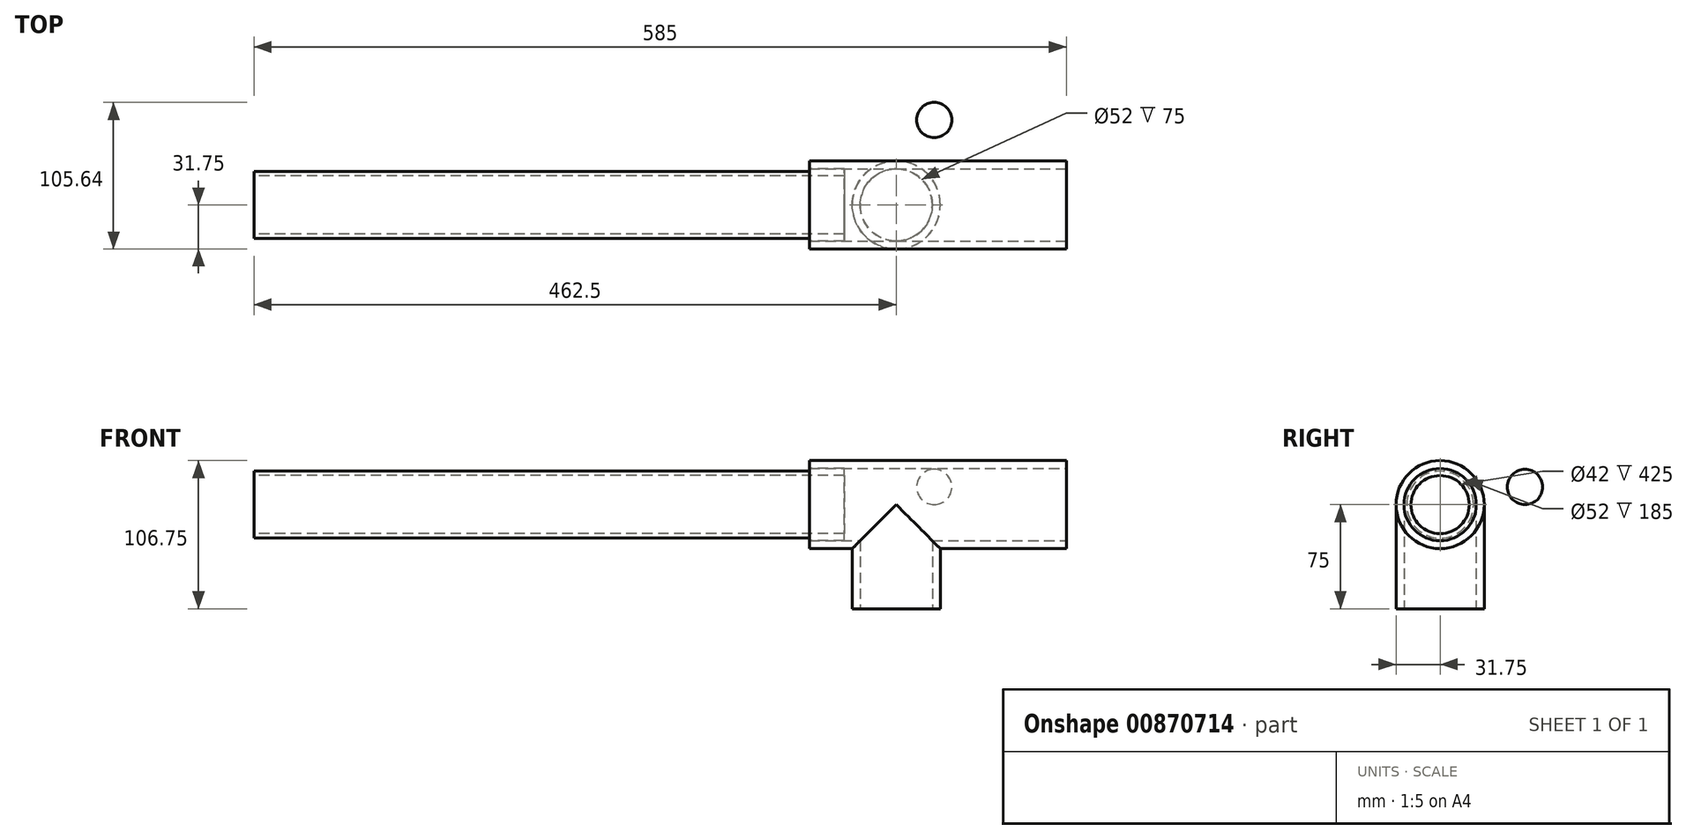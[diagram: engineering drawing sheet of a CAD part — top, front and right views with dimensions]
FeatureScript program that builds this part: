
annotation { "Feature Type Name" : "Feature", "Feature Type Description" : "" }
export const myFeature = defineFeature(function(context is Context, id is Id, definition is map)
    precondition{}
    {
        {
            var Q0;
            Q0=qCreatedBy(makeId("Right.planeOp"),FACE);
            var sketch = newSketch(context, id + "F0", { "sketchPlane" : qUnion([Q0])});
            skCircle(sketch, "E0", {"center": v(0, 0) * mm, "radius": 26 * mm});
            skCircle(sketch, "E1", {"center": v(0, 0) * mm, "radius": 31.75 * mm});
            skSolve(sketch);
        }
        {
            var Q0;
            Q0=makeQuery(id+"F0.imprint","IMPRINT",FACE,{"disambiguationData":[TD([[makeQuery(id+"F0.imprint","IMPRINT",EDGE,{"derivedFrom":sQuery(id+"F0.wireOp",EDGE,"E0")}),-1.0]])]});
            extrude(context, id + "F1", {"entities" : qUnion([Q0]), "oppositeDirection" : true, "depth" : 25 * mm, "offsetDistance" : 25 * mm});
        }
        {
            var Q0;
            Q0=makeQuery(id+"F1.opExtrude","CAP_FACE",FACE,{"disambiguationData":[OSD([sQuery(id+"F0.wireOp",EDGE,"E0"),sQuery(id+"F0.wireOp",EDGE,"E1")])],"isStart":false});
            extrude(context, id + "F2", {"entities" : qUnion([Q0]), "operationType" : NewBodyOperationType.ADD, "depth" : 75 * mm, "offsetDistance" : 25 * mm});
        }
        {
            var Q0;
            Q0=makeQuery(id+"F2.opExtrude","CAP_FACE",FACE,{"disambiguationData":[OSD([sQuery(id+"F0.wireOp",EDGE,"E0"),sQuery(id+"F0.wireOp",EDGE,"E1")])],"isStart":false});
            extrude(context, id + "F3", {"entities" : qUnion([Q0]), "operationType" : NewBodyOperationType.ADD, "depth" : 25 * mm, "offsetDistance" : 25 * mm});
        }
        {
            var Q0;
            Q0=qCreatedBy(makeId("Top.planeOp"),FACE);
            var sketch = newSketch(context, id + "F4", { "sketchPlane" : qUnion([Q0])});
            skCircle(sketch, "E2", {"center": v(-62.5, 0) * mm, "radius": 31.75 * mm});
            skSolve(sketch);
        }
        {
            var Q0;
            Q0=qCreatedBy(makeId("Top.planeOp"),FACE);
            var sketch = newSketch(context, id + "F5", { "sketchPlane" : qUnion([Q0])});
            skCircle(sketch, "E3", {"center": v(-62.5, 0) * mm, "radius": 26 * mm});
            skSolve(sketch);
        }
        {
            var Q0;
            Q0=makeQuery(id+"F3.opExtrude","CAP_FACE",FACE,{"disambiguationData":[OSD([sQuery(id+"F0.wireOp",EDGE,"E0"),sQuery(id+"F0.wireOp",EDGE,"E1")])],"isStart":false});
            var sketch = newSketch(context, id + "F6", { "sketchPlane" : qUnion([Q0])});
            skCircle(sketch, "E4", {"center": v(0, 0) * mm, "radius": 26 * mm});
            skSolve(sketch);
        }
        {
            var Q0;
            Q0=makeQuery(id+"F6.imprint","IMPRINT",FACE,{"disambiguationData":[TD([[makeQuery(id+"F6.imprint","IMPRINT",EDGE,{"derivedFrom":sQuery(id+"F6.wireOp",EDGE,"E4")}),-1.0]])]});
            extrude(context, id + "F7", {"entities" : qUnion([Q0]), "operationType" : NewBodyOperationType.REMOVE, "oppositeDirection" : true, "depth" : 150 * mm, "offsetDistance" : 25 * mm});
        }
        {
            var Q0;
            Q0=makeQuery(id+"F1.opExtrude","CAP_FACE",FACE,{"disambiguationData":[OSD([sQuery(id+"F0.wireOp",EDGE,"E0"),sQuery(id+"F0.wireOp",EDGE,"E1")])],"isStart":true});
            extrude(context, id + "F8", {"entities" : qUnion([Q0]), "operationType" : NewBodyOperationType.ADD, "depth" : 75 * mm, "offsetDistance" : 25 * mm});
        }
        {
            var Q0;
            Q0=makeQuery(id+"F5.imprint","IMPRINT",FACE,{"disambiguationData":[TD([[makeQuery(id+"F5.imprint","IMPRINT",EDGE,{"derivedFrom":sQuery(id+"F5.wireOp",EDGE,"E3")}),1.0]])]});
            var Q1;
            Q1=makeQuery(id+"F4.imprint","IMPRINT",FACE,{"disambiguationData":[TD([[makeQuery(id+"F4.imprint","IMPRINT",EDGE,{"derivedFrom":sQuery(id+"F4.wireOp",EDGE,"E2")}),1.0]])]});
            extrude(context, id + "F9", {"entities" : qUnion([Q0, Q1]), "operationType" : NewBodyOperationType.ADD, "oppositeDirection" : true, "depth" : 75 * mm, "offsetDistance" : 25 * mm});
        }
        {
            var Q0;
            Q0=makeQuery(id+"F9.opExtrude","CAP_FACE",FACE,{"disambiguationData":[OSD([sQuery(id+"F4.wireOp",EDGE,"E2")])],"isStart":false});
            var sketch = newSketch(context, id + "F10", { "sketchPlane" : qUnion([Q0])});
            skCircle(sketch, "E5", {"center": v(-62.5, 0) * mm, "radius": 26 * mm});
            skSolve(sketch);
        }
        {
            var Q0;
            Q0 = qSketchRegion(id + "F10", true);
            extrude(context, id + "F11", {"entities" : qUnion([Q0]), "operationType" : NewBodyOperationType.REMOVE, "oppositeDirection" : true, "depth" : 75 * mm, "offsetDistance" : 25 * mm});
        }
        {
            var Q0;
            Q0=makeQuery(id+"F3.opExtrude","CAP_FACE",FACE,{"disambiguationData":[OSD([sQuery(id+"F0.wireOp",EDGE,"E0"),sQuery(id+"F0.wireOp",EDGE,"E1")])],"isStart":false});
            var sketch = newSketch(context, id + "F12", { "sketchPlane" : qUnion([Q0])});
            skCircle(sketch, "E6", {"center": v(0, 0) * mm, "radius": 26 * mm});
            skSolve(sketch);
        }
        {
            var Q0;
            Q0=makeQuery(id+"F12.imprint","IMPRINT",FACE,{"disambiguationData":[TD([[makeQuery(id+"F12.imprint","IMPRINT",EDGE,{"derivedFrom":sQuery(id+"F12.wireOp",EDGE,"E6")}),-1.0]])]});
            extrude(context, id + "F13", {"entities" : qUnion([Q0]), "operationType" : NewBodyOperationType.REMOVE, "oppositeDirection" : true, "depth" : 200 * mm, "offsetDistance" : 25 * mm});
        }
        {
            var Q0;
            Q0=makeQuery(id+"F3.opExtrude","CAP_FACE",FACE,{"disambiguationData":[OSD([sQuery(id+"F0.wireOp",EDGE,"E0"),sQuery(id+"F0.wireOp",EDGE,"E1")])],"isStart":false});
            var sketch = newSketch(context, id + "F14", { "sketchPlane" : qUnion([Q0])});
            skCircle(sketch, "E7", {"center": v(0, 0) * mm, "radius": 24.13 * mm});
            skCircle(sketch, "E8", {"center": v(0, 0) * mm, "radius": 21 * mm});
            skSolve(sketch);
        }
        {
            var Q0;
            Q0=makeQuery(id+"F14.imprint","IMPRINT",FACE,{"disambiguationData":[TD([[makeQuery(id+"F14.imprint","IMPRINT",EDGE,{"derivedFrom":sQuery(id+"F14.wireOp",EDGE,"E7")}),1.0]])]});
            var Q1;
            Q1=makeQuery(id+"F14.imprint","IMPRINT",FACE,{"disambiguationData":[TD([[makeQuery(id+"F14.imprint","IMPRINT",EDGE,{"derivedFrom":sQuery(id+"F14.wireOp",EDGE,"E7")}),-1.0]])]});
            extrude(context, id + "F15", {"entities" : qUnion([Q0, Q1]), "oppositeDirection" : true, "depth" : 25 * mm, "offsetDistance" : 25 * mm});
        }
        {
            var Q0;
            Q0=makeQuery(id+"F15.opExtrude","CAP_FACE",FACE,{"disambiguationData":[OSD([sQuery(id+"F0.wireOp",EDGE,"E0"),sQuery(id+"F14.wireOp",EDGE,"E8")])],"isStart":true});
            var sketch = newSketch(context, id + "F16", { "sketchPlane" : qUnion([Q0])});
            skCircle(sketch, "E9", {"center": v(0, 0) * mm, "radius": 24.13 * mm});
            skSolve(sketch);
        }
        {
            var Q0;
            Q0=makeQuery(id+"F16.imprint","IMPRINT",FACE,{"disambiguationData":[TD([[makeQuery(id+"F16.imprint","IMPRINT",EDGE,{"derivedFrom":sQuery(id+"F16.wireOp",EDGE,"E9")}),1.0]])]});
            extrude(context, id + "F17", {"entities" : qUnion([Q0]), "operationType" : NewBodyOperationType.ADD, "depth" : 400 * mm, "offsetDistance" : 25 * mm});
        }
        {
            var Q0;
            Q0=qCreatedBy(makeId("Top.planeOp"),FACE);
            var sketch = newSketch(context, id + "F18", { "sketchPlane" : qUnion([Q0])});
            skCircle(sketch, "E10", {"center": v(-35.15, 61.2) * mm, "radius": 12.7 * mm});
            skSolve(sketch);
        }
        {
            var Q0;
            Q0 = qSketchRegion(id + "F18", true);
            extrude(context, id + "F19", {"entities" : qUnion([Q0]), "depth" : 25.4 * mm, "offsetDistance" : 25 * mm});
        }
        {
            var Q0;
            Q0=makeQuery(id+"F19.opExtrude","CAP_EDGE",EDGE,{"disambiguationData":[OSD([sQuery(id+"F18.wireOp",EDGE,"E10")])],"isStart":false});
            var Q1;
            Q1=makeQuery(id+"F19.opExtrude","CAP_EDGE",EDGE,{"disambiguationData":[OSD([sQuery(id+"F18.wireOp",EDGE,"E10")])],"isStart":true});
            fillet(context, id + "F20", {"entities" : qUnion([Q0, Q1]), "radius" : 12.7 * mm, "tangentPropagation" : true, "allowEdgeOverflow" : false});
        }
        {
            var Q0;
            Q0=qCreatedBy(makeId("Right.planeOp"),FACE);
            var sketch = newSketch(context, id + "F21", { "sketchPlane" : qUnion([Q0])});
            skCircle(sketch, "E11", {"center": v(-100, 0) * mm, "radius": 9.53 * mm});
            skCircle(sketch, "E12", {"center": v(-100, 0) * mm, "radius": 12.5 * mm});
            skSolve(sketch);
        }
        {
            var Q0;
            Q0 = qSketchRegion(id + "F21", true);
            extrude(context, id + "F22", {"entities" : qUnion([Q0]), "oppositeDirection" : true, "depth" : 25 * mm, "offsetDistance" : 25 * mm});
        }
        {
            var Q0;
            Q0=makeQuery(id+"F22.opExtrude","CAP_FACE",FACE,{"disambiguationData":[OSD([sQuery(id+"F21.wireOp",EDGE,"E11"),sQuery(id+"F21.wireOp",EDGE,"E12")])],"isStart":false});
            var sketch = newSketch(context, id + "F23", { "sketchPlane" : qUnion([Q0])});
            skCircle(sketch, "E13", {"center": v(100, 0) * mm, "radius": 17.5 * mm});
            skCircle(sketch, "E14", {"center": v(100, 0) * mm, "radius": 12.5 * mm});
            skSolve(sketch);
        }
        {
            var Q0;
            Q0 = qSketchRegion(id + "F23", true);
            extrude(context, id + "F24", {"entities" : qUnion([Q0]), "depth" : 25 * mm, "offsetDistance" : 25 * mm});
        }
        {
            var Q0;
            Q0=makeQuery(id+"F24.opExtrude","CAP_FACE",FACE,{"disambiguationData":[OSD([sQuery(id+"F23.wireOp",EDGE,"E13"),sQuery(id+"F23.wireOp",EDGE,"E14")])],"isStart":true});
            extrude(context, id + "F25", {"entities" : qUnion([Q0]), "depth" : 5 * mm, "offsetDistance" : 25 * mm});
        }
        {
            var Q0;
            Q0=makeQuery(id+"F22.opExtrude","CAP_FACE",FACE,{"disambiguationData":[OSD([sQuery(id+"F21.wireOp",EDGE,"E11"),sQuery(id+"F21.wireOp",EDGE,"E12")])],"isStart":false});
            var sketch = newSketch(context, id + "F26", { "sketchPlane" : qUnion([Q0])});
            skCircle(sketch, "E15", {"center": v(100, 0) * mm, "radius": 5 * mm});
            skSolve(sketch);
        }
        {
            var Q0;
            Q0=makeQuery(id+"F26.imprint","IMPRINT",FACE,{"disambiguationData":[TD([[makeQuery(id+"F26.imprint","IMPRINT",EDGE,{"derivedFrom":sQuery(id+"F26.wireOp",EDGE,"E15")}),-1.0]])]});
            var Q1;
            Q1=makeQuery(id+"F26.imprint","IMPRINT",FACE,{"disambiguationData":[TD([[makeQuery(id+"F26.imprint","IMPRINT",EDGE,{"derivedFrom":makeQuery(id+"F22.opExtrude","CAP_EDGE",EDGE,{"disambiguationData":[OSD([sQuery(id+"F21.wireOp",EDGE,"E11")])],"isStart":false})}),1.0]])]});
            extrude(context, id + "F27", {"entities" : qUnion([Q0, Q1]), "depth" : 5 * mm, "offsetDistance" : 25 * mm});
        }
        {
            var Q0;
            Q0=makeQuery(id+"F24.opExtrude","CAP_FACE",FACE,{"disambiguationData":[OSD([sQuery(id+"F23.wireOp",EDGE,"E13"),sQuery(id+"F23.wireOp",EDGE,"E14")])],"isStart":false});
            extrude(context, id + "F28", {"entities" : qUnion([Q0]), "operationType" : NewBodyOperationType.ADD, "depth" : 10 * mm, "offsetDistance" : 25 * mm});
        }
        {
            var Q0;
            Q0=makeQuery(id+"F8.opExtrude","CAP_FACE",FACE,{"disambiguationData":[OSD([sQuery(id+"F0.wireOp",EDGE,"E0"),sQuery(id+"F0.wireOp",EDGE,"E1")])],"isStart":false});
            var sketch = newSketch(context, id + "F29", { "sketchPlane" : qUnion([Q0])});
            skCircle(sketch, "E16", {"center": v(0, 0) * mm, "radius": 9.53 * mm});
            skSolve(sketch);
        }
        {
            var Q0;
            Q0=makeQuery(id+"F29.imprint","IMPRINT",FACE,{"disambiguationData":[TD([[makeQuery(id+"F29.imprint","IMPRINT",EDGE,{"derivedFrom":makeQuery(id+"F8.opExtrude","CAP_EDGE",EDGE,{"disambiguationData":[OSD([sQuery(id+"F0.wireOp",EDGE,"E0")])],"isStart":false})}),-1.0]])]});
            var Q1;
            Q1=makeQuery(id+"F29.imprint","IMPRINT",FACE,{"disambiguationData":[TD([[makeQuery(id+"F29.imprint","IMPRINT",EDGE,{"derivedFrom":sQuery(id+"F29.wireOp",EDGE,"E16")}),-1.0]])]});
            extrude(context, id + "F30", {"entities" : qUnion([Q0, Q1]), "operationType" : NewBodyOperationType.ADD, "depth" : 10 * mm, "offsetDistance" : 25 * mm});
        }
        {
            var Q0;
            Q0=makeQuery(id+"F27.opExtrude","SWEPT_BODY",BODY,{"disambiguationData":[OSD([sQuery(id+"F21.wireOp",EDGE,"E12"),sQuery(id+"F26.wireOp",EDGE,"E15")])]});
            deleteBodies(context, id + "F31", {"entities" : qUnion([Q0])});
        }
        {
            var Q0;
            Q0=makeQuery(id+"F25.opExtrude","SWEPT_BODY",BODY,{"disambiguationData":[OSD([sQuery(id+"F23.wireOp",EDGE,"E13"),sQuery(id+"F23.wireOp",EDGE,"E14")])]});
            var Q1;
            Q1=makeQuery(id+"F24.opExtrude","SWEPT_BODY",BODY,{"disambiguationData":[OSD([sQuery(id+"F23.wireOp",EDGE,"E13"),sQuery(id+"F23.wireOp",EDGE,"E14")])]});
            deleteBodies(context, id + "F32", {"entities" : qUnion([Q0, Q1])});
        }
        {
            var Q0;
            Q0=makeQuery(id+"F22.opExtrude","SWEPT_BODY",BODY,{"disambiguationData":[OSD([sQuery(id+"F21.wireOp",EDGE,"E11"),sQuery(id+"F21.wireOp",EDGE,"E12")])]});
            deleteBodies(context, id + "F33", {"entities" : qUnion([Q0])});
        }
        {
            var Q0;
            Q0=makeQuery(id+"F30.opExtrude","CAP_FACE",FACE,{"disambiguationData":[OSD([sQuery(id+"F0.wireOp",EDGE,"E1"),sQuery(id+"F29.wireOp",EDGE,"E16")])],"isStart":false});
            extrude(context, id + "F34", {"entities" : qUnion([Q0]), "operationType" : NewBodyOperationType.REMOVE, "oppositeDirection" : true, "depth" : 25 * mm, "offsetDistance" : 25 * mm});
        }
    });
